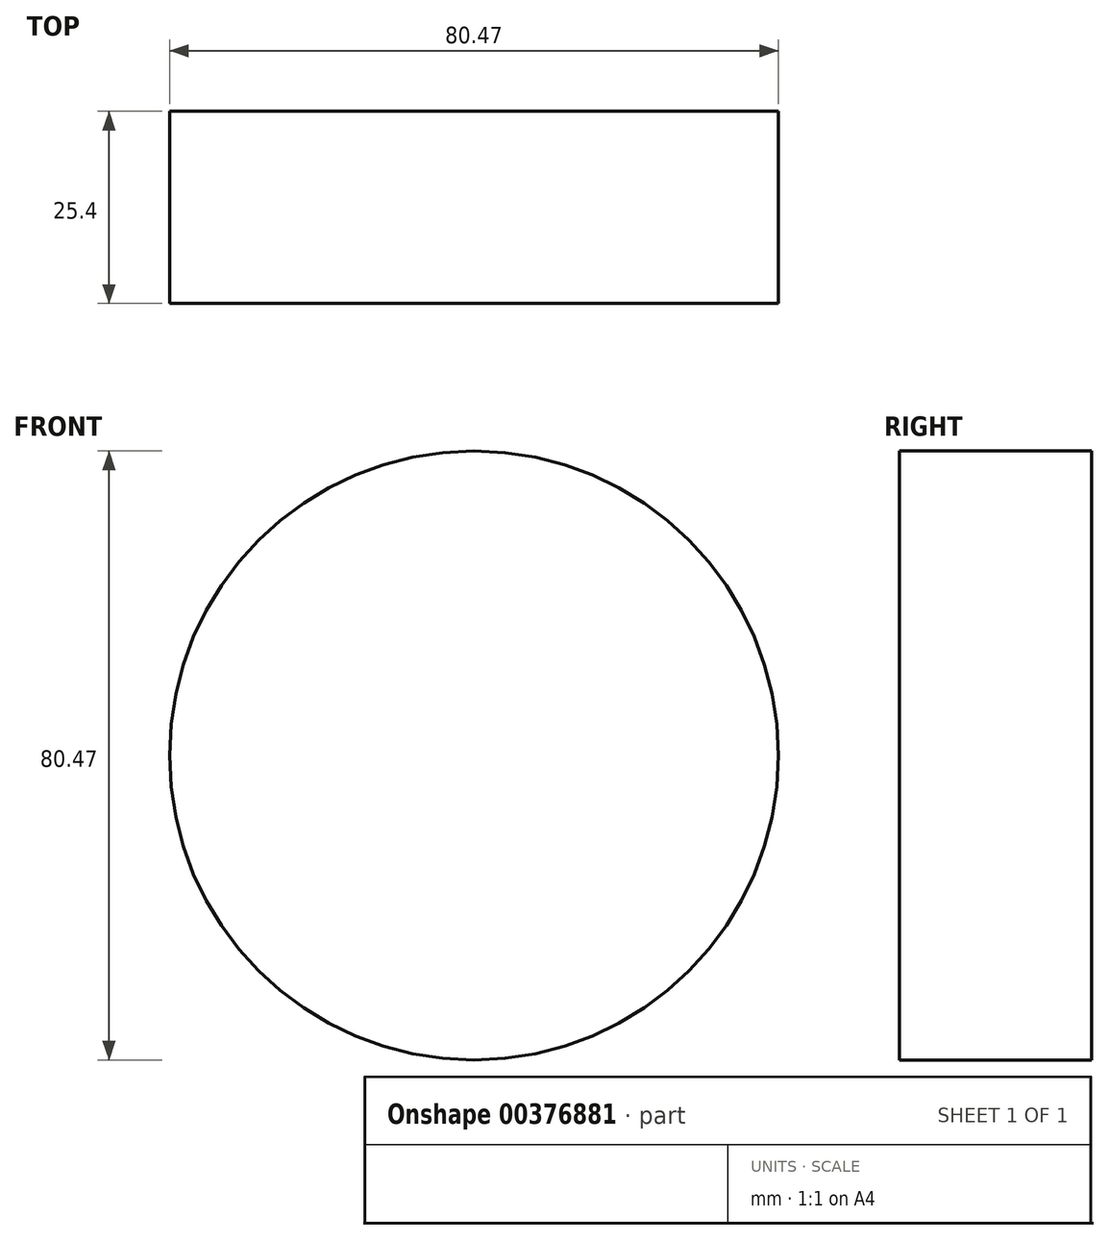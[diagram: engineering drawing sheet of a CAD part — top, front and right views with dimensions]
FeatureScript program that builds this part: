
annotation { "Feature Type Name" : "Feature", "Feature Type Description" : "" }
export const myFeature = defineFeature(function(context is Context, id is Id, definition is map)
    precondition{}
    {
        {
            var Q0;
            Q0=qCreatedBy(makeId("Front.planeOp"),FACE);
            var sketch = newSketch(context, id + "F0", { "sketchPlane" : qUnion([Q0])});
            skCircle(sketch, "E0", {"center": v(-18.37, 116.3) * mm, "radius": 40.24 * mm});
            skSolve(sketch);
        }
        {
            var Q0;
            Q0 = qSketchRegion(id + "F0", true);
            extrude(context, id + "F1", {"entities" : qUnion([Q0]), "depth" : 25.4 * mm});
        }
    });
